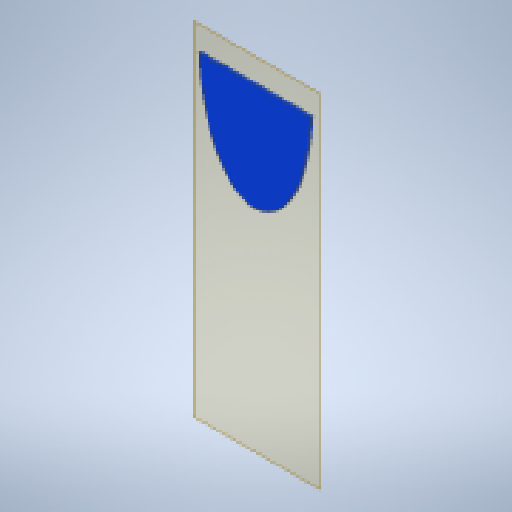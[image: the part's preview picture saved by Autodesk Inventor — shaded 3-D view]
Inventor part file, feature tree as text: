
AUTODESK INVENTOR PART (.ipt)
format: ipt  version: 2023 (Build 270158030, 158C)  size: 249,344 bytes
history: native  units: mm
features: other x3, plane x1, extrude x1, sketch x1, reference x1
ambient origin geometry x8: Origin, YZ Plane, XZ Plane, XY Plane, X Axis, Y Axis, Z Axis, Center Point
bodies: Solid1 (feature_tree)
feature tree (7):
  plane  "Work Plane1"
  extrude  "Extrusion1"  Depth=900.0mm
  sketch  "Sketch1"  dims[d0=700.0mm d1=900.0mm d2=350.0mm d3=350.0mm d4=40.0mm d5=40.0mm d6=15.0mm d7=0.0mm d8=20.0mm]
  reference  "Reference1"
  other  "<userpath>\Documents\0004-inventor\3D-CAD-main\primary-engineer-bench.iam"
  other  "primary-engineer-bench.iam"
  other  "bed-base:1"
